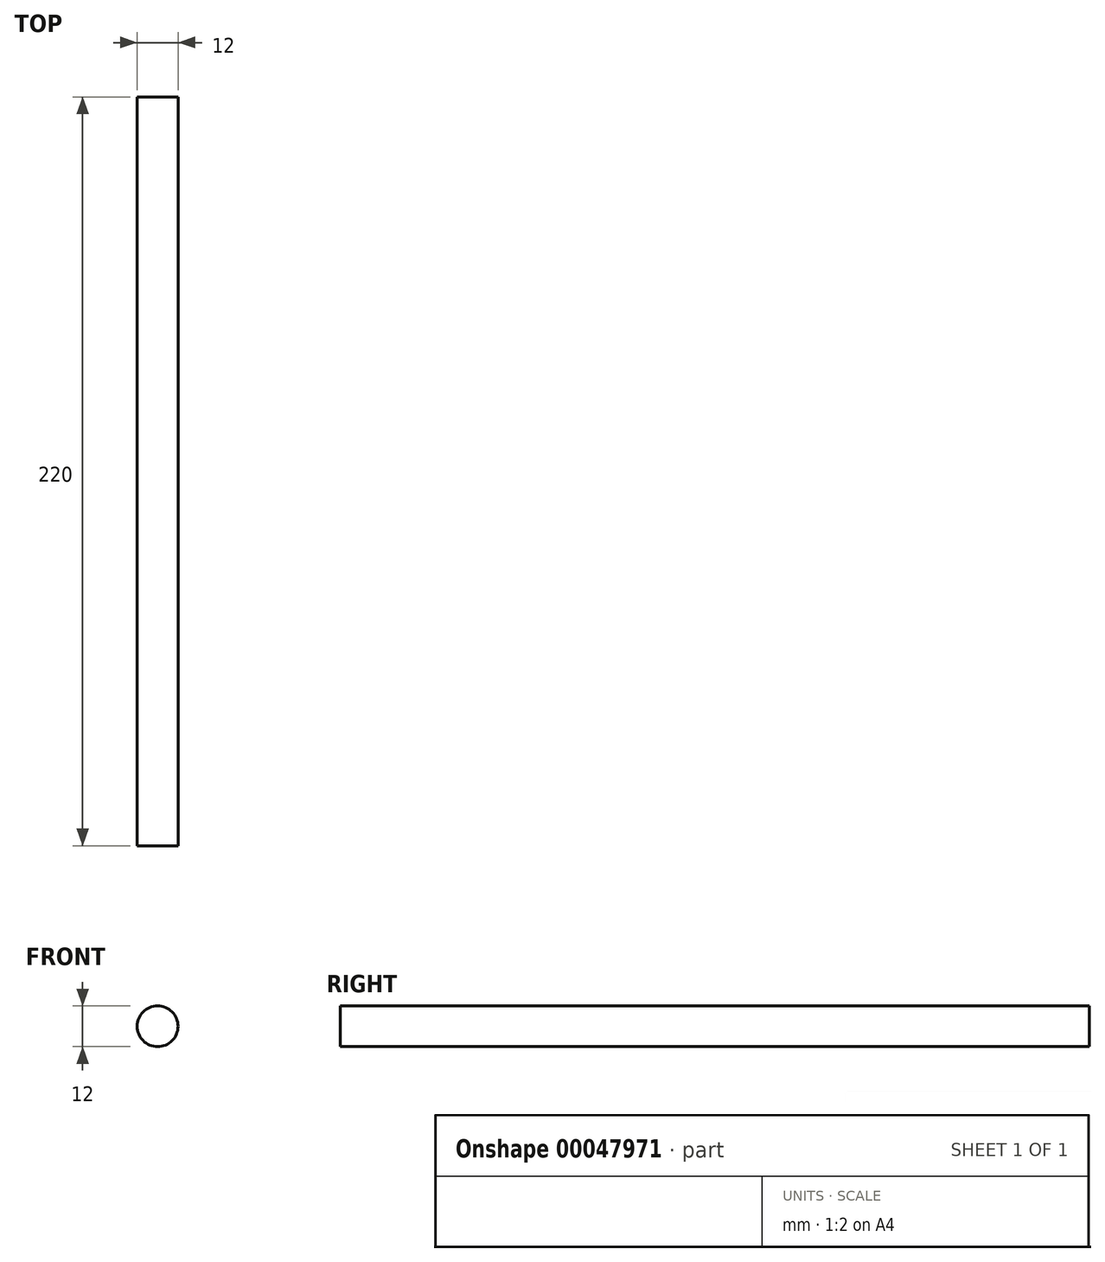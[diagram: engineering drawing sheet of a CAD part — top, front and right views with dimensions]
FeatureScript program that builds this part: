
annotation { "Feature Type Name" : "Feature", "Feature Type Description" : "" }
export const myFeature = defineFeature(function(context is Context, id is Id, definition is map)
    precondition{}
    {
        {
            var Q0;
            Q0=qCreatedBy(makeId("Front.planeOp"),FACE);
            var sketch = newSketch(context, id + "F0", { "sketchPlane" : qUnion([Q0])});
            skCircle(sketch, "E0", {"center": v(0, 0) * mm, "radius": 6 * mm});
            skSolve(sketch);
        }
        {
            var Q0;
            Q0=makeQuery(id+"F0.imprint","IMPRINT",FACE,{"disambiguationData":[TD([[makeQuery(id+"F0.imprint","IMPRINT",EDGE,{"derivedFrom":sQuery(id+"F0.wireOp",EDGE,"E0")}),1.0]])]});
            extrude(context, id + "F1", {"entities" : qUnion([Q0]), "depth" : 220 * mm, "symmetric" : true});
        }
    });
